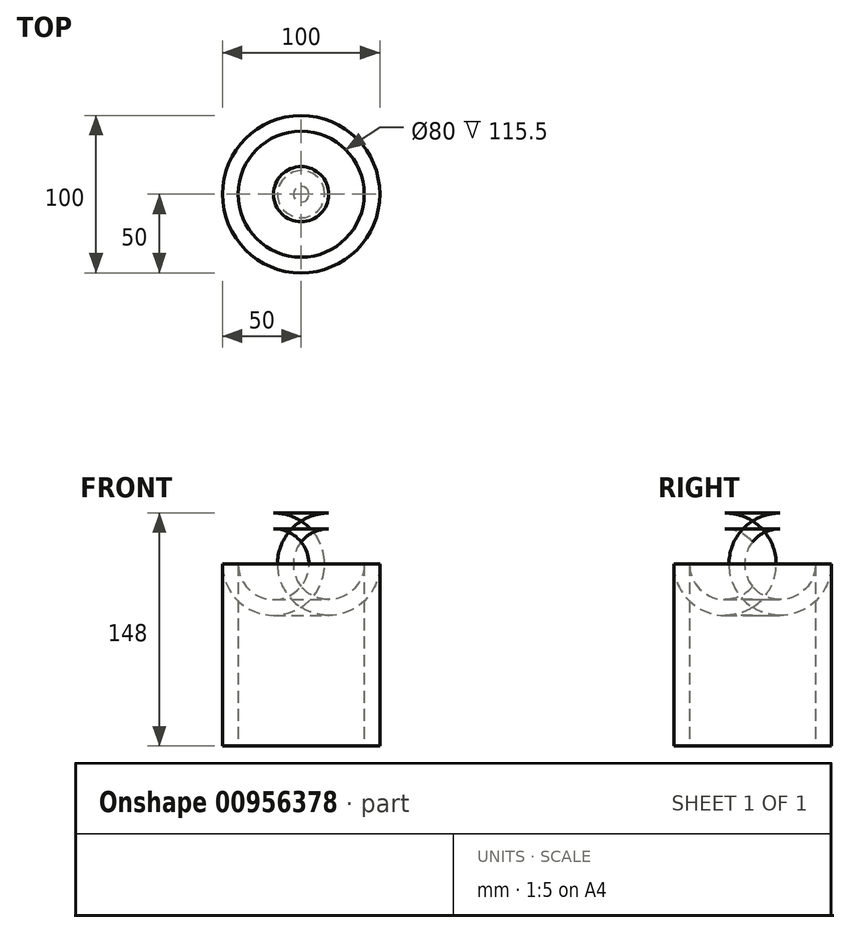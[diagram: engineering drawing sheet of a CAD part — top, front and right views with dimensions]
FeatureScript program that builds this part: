
annotation { "Feature Type Name" : "Feature", "Feature Type Description" : "" }
export const myFeature = defineFeature(function(context is Context, id is Id, definition is map)
    precondition{}
    {
        {
            var Q0;
            Q0=qCreatedBy(makeId("Front.planeOp"),FACE);
            var sketch = newSketch(context, id + "F0", { "sketchPlane" : qUnion([Q0])});
            skLineSegment(sketch, "E0.left", {"start": v(-50, -59.53) * mm, "end": v(-50, 55.97) * mm});
            skPoint(sketch, "E0.middle", {"position": v(0, 0) * mm});
            skArc(sketch, "E1", {"start": v(-17.5, 88.47) * mm, "mid": v(-40.48, 78.95) * mm, "end": v(-50, 55.97) * mm});
            skLineSegment(sketch, "E2", {"start": v(-17.5, 88.47) * mm, "end": v(0, 88.47) * mm});
            skLineSegment(sketch, "E3.1", {"start": v(-40, -59.53) * mm, "end": v(-40, 55.97) * mm});
            skArc(sketch, "E3.2", {"start": v(-17.5, 78.47) * mm, "mid": v(-33.4, 71.88) * mm, "end": v(-40, 55.97) * mm});
            skLineSegment(sketch, "E3.3", {"start": v(-17.5, 78.47) * mm, "end": v(0, 78.47) * mm});
            skLineSegment(sketch, "E4", {"start": v(-50, -59.53) * mm, "end": v(-40, -59.53) * mm});
            skLineSegment(sketch, "E5", {"start": v(0, 0) * mm, "end": v(0, 145.4) * mm, "construction": true});
            skPoint(sketch, "E6.MirrorCS.end.orphan", {"position": v(40, 55.97) * mm});
            skLineSegment(sketch, "E7", {"start": v(0, 88.47) * mm, "end": v(0, 78.47) * mm});
            skSolve(sketch);
        }
        {
            var Q0;
            Q0=makeQuery(id+"F0.imprint","IMPRINT",FACE,{"disambiguationData":[TD([[makeQuery(id+"F0.imprint","IMPRINT",EDGE,{"derivedFrom":sQuery(id+"F0.wireOp",EDGE,"E0.left")}),-1.0]])]});
            var Q1;
            Q1=sQuery(id+"F0.wireOp",EDGE,"E5");
            revolve(context, id + "F1", {"surfaceOperationType" : NewSurfaceOperationType.NEW, "entities" : qUnion([Q0]), "axis" : qUnion([Q1]), "revolveType" : RevolveType.FULL});
        }
    });
